# Revit family: Lavamanos Marsella 2
name_source: partatom
category: Aparatos sanitarios
revit_build: Autodesk Revit 2016 (Build: 20151007_0715(x64)
units: mm (PartAtom-declared; Revit-internal decimal feet)

## family parameters
Anfitrión = Cara
Compartido = No
Corte con vacíos al cargar = No
Cota de conector redondo = Diámetro de uso
Número OmniClass = 23.45.55.00
Punto de cálculo de habitación = No
Tipo de pieza = Normal
Título OmniClass = Sanitary Faucets, Wastes

## types (1)
- Lavamanos Marsella 2
    Acabado = Brillante
    Altura Nominal = 205 mm
    Ancho Nominal = 508 mm
    Color = Blanco
    Cumplimiento de Norma = Cumple con las normas Icontec NTC 920 y ASME / ASME / ANSI A112.19.2
    Descripción = Diseño contemporaneo, que permite combinar con gran cantidad de sanitarios, Agujero integral de drenaje que evita el rebose, Agujeros insinuados que permiten escoger diferentes opciones de griferia
    Descripción de la garantía = Garantia limitada Corona de por vida
    Diametro de conexión sanitaria = 2"
    Diámetro de conexión entrada = 1/2"
    Elevación por defecto = 1219 mm
    Fabricante = Corona
    Forma = Ovalado
    Imagen de tipo = <Ninguno>
    Información del producto = https://www.corona.co
    Logitud Nominal = 450 mm
    Material = Ceramica_Corona_Blanco
    Material de Fabricacion = Porcelana Sanitaria
    Nombre = Lavamanos de sobreponer en porcelana Marsella
    Nombre del Fabricante = Colceramica S.A.S
    Número Modelo = 01301
    Responsable Garantías Partes = www.corona.com.co
    Tamaño = 508 x 450 x 205 mm
    Tipo de Activo = Fijo
    URL = https://www.corona.co
